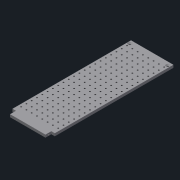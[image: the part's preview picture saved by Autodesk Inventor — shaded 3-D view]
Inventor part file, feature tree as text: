
AUTODESK INVENTOR PART (.ipt)
format: ipt  version: 2021.1 (Build 251245000, 245)  size: 316,928 bytes
history: native  units: in
note: dims shown in document units (in); Inventor stores cm internally (conversion verified against a paired STEP export)
features: sketch x6, hole x4, extrude x2, pattern_linear x2, projected_geometry x1
ambient origin geometry x8: Origin, YZ Plane, XZ Plane, XY Plane, X Axis, Y Axis, Z Axis, Center Point
bodies: Solid1 (feature_tree)
feature tree (15):
  extrude  "Base"  Depth=11.75in
  hole  "Threaded Mount Holes"  [1 undecoded]
  pattern_linear  "Threaded Holes"  Count1=21 Spacing1=0.5in
  hole  "Leg Mount Holes"  [1 undecoded]
  pattern_linear  "Rectangular Pattern2"  Count1=2 Spacing1=3.592in
  extrude  "Leg Cut Out"  Depth=3.342in
  hole  "Leg Mount Hole 1"  [1 undecoded]
  hole  "Leg Mount Hole 2"  [1 undecoded]
  sketch  "Sketch1"  dims[d0=4.0in d1=11.75in]
  sketch  "Sketch7"  dims[d2=0.25in d3=0.0in d35=0.625in]
  projected_geometry  "Projected Loop1"
  sketch  "Sketch8"  dims[d36=0.25in]
  sketch  "Sketch9"  dims[d37=0.1276in d38=0.315in d39=0.175in d40=0.25in d41=0.5635in d42=0.465in d43=0.8108in d44=8.2677in d46=0.5in]
  sketch  "Sketch10"  dims[d47=3.1496in d49=0.5in d50=0.305in]
  sketch  "Sketch11"  dims[d51=0.204in d52=0.169in d53=0.315in d54=0.37in d55=0.134in d56=90.0deg d57=0.465in d58=0.8108in d62=0.7874in d64=3.592in d65=3.342in d66=0.329in d67=10.89in d71=10.89in d72=0.25in d73=0.0in d74=0.25in d75=0.125in d76=0.128in d77=0.5in d78=0.18in d79=0.134in d80=90.0deg d81=1.0in d82=0.8108in d83=0.25in d84=0.125in d85=0.128in d86=0.5in d87=0.18in d88=0.134in d89=90.0deg d90=1.0in d91=0.8108in]
note: 4 required parameter values undecoded (feature->parameter linkage not recoverable at this tier; creation-order binding heuristic only, values carry confidence <= 0.55)
